# Revit family: 215W x 440H R.C. Beam
name_source: partatom
category: Generic Models
units: mm (PartAtom-declared; Revit-internal decimal feet)

## family parameters
Always vertical = Yes
Can host rebar = No
Cut with Voids When Loaded = No
Part Type = Normal
Room Calculation Point = No
Round Connector Dimension = Use Diameter
Shared = No
Work Plane-Based = No

## types (1)
- 215W x 440H R.C. Beam
    Characteristics Deflection Under Load = Dependant on Length.
    Characteristics of Reinforcing Steel = Ultimate Tensile Strength (UTS) 650Mpa. Tensile Yield Strength: 500Mpa.
    Compressive Strength of Concrete = 40N/mm²
    Construction Tolerance Class = I.S. EN 13225:2013
    Construction Type = Precast
    Dangerous Substances = No Exposure.
    Default Elevation = 0 mm  [stored 0 ft]
    Description = 215W x 440H R.C. Beam
    Detailing = As per design specification and product drawings.
    Dimension Accuracy Class = I.S. EN 13225:2013
    Durability against Corrosion = Design specification and critical dimensions as per product drawings.
    Keynote = The information contained is the sole property of KPC Ltd., any reproduction in part or whole without permission of KPC Ltd. is prohibited.
    Length Options = All sizes available on request.
    Load Bearing = Yes
    Manufacturer = Killeshal Precast Concrete Ltd.
    Mechanical Resistance = Method 3. Design specification.
    Model = L/308 Concrete Beam
    Nominal Cover to Main Bar = 40mm
    Notified Body = National Standards Authority of Ireland (NSAI).
    Resistance to Fire = Method 3. Design specification.
    Service Life = 0.000000
    Shape = Rectangular
    Size = 215mm x 440mm
    Slope = 0.00°
    Span = Beam Length
    Type Comments = Visit our website for a full list of available products.
    Types = Single
    URL = www.killeshal.com
    Weight = 228Kg/m

note: [stored X ft] marks values corroborated as IEEE doubles in the binary element streams (Revit-internal decimal feet)

## geometry (parser evidence)
native form markers: Sweep x3
no freeform markers — native parametric forms only
